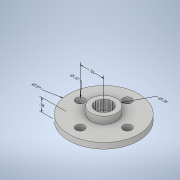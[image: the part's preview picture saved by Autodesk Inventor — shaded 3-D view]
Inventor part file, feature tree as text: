
AUTODESK INVENTOR PART (.ipt)
format: ipt  version: 2022 (Build 260153000, 153)  size: 219,136 bytes
history: native  units: in
note: dims shown in document units (in); Inventor stores cm internally (conversion verified against a paired STEP export)
features: other x6, extrude x5, sketch x5, pattern_circular x2
ambient origin geometry x8: Origin, YZ Plane, XZ Plane, XY Plane, X Axis, Y Axis, Z Axis, Center Point
bodies: Solid1 (feature_tree)
feature tree (18):
  other  "Annotations"
  extrude  "Extrusion1"  Depth=0.3543in
  extrude  "Extrusion2"  Depth=0.1181in
  extrude  "Extrusion3"  Depth=0.0787in
  extrude  "Extrusion4"  Depth=0.1772in
  pattern_circular  "Circular Pattern1"  [2 undecoded]
  extrude  "Extrusion5"  Depth=0.1772in
  pattern_circular  "Circular Pattern2"  [2 undecoded]
  sketch  "Sketch1"  dims[d0=0.9685in d1=0.3543in]
  sketch  "Sketch4"  dims[d10=0.1772in d11=0.0in d12=0.7874in d13=0.3543in d14=0.2165in d15=0.1181in]
  sketch  "Sketch5"  dims[d16=0.0394in d17=0.0in d18=0.6535in d19=0.1181in d20=0.0394in d21=0.0in d22=1.5748in d23=360.0deg d25=0.2362in d26=0.0495in d27=0.0989in d28=0.0394in d29=0.0in d30=9.8425in d31=360.0deg d33=0.0732in d34=0.9685in d35=0.3268in d36=1.6667in d37=0.3543in d38=0.3305in d39=0.2482in d40=0.1772in d41=2.31in d42=0.1181in]
  sketch  "Sketch2"  dims[d2=0.2165in d3=0.1181in]
  sketch  "Sketch3"  dims[d4=0.0787in d5=0.0in d6=0.7874in d7=0.3543in d8=0.2165in d9=0.1181in]
  other  "Diameter Dimension 1"
  other  "Linear Dimension 1"
  other  "Diameter Dimension 2"
  other  "Linear Dimension 2"
  other  "Diameter Dimension 3"
note: 4 required parameter values undecoded (feature->parameter linkage not recoverable at this tier; creation-order binding heuristic only, values carry confidence <= 0.55)
